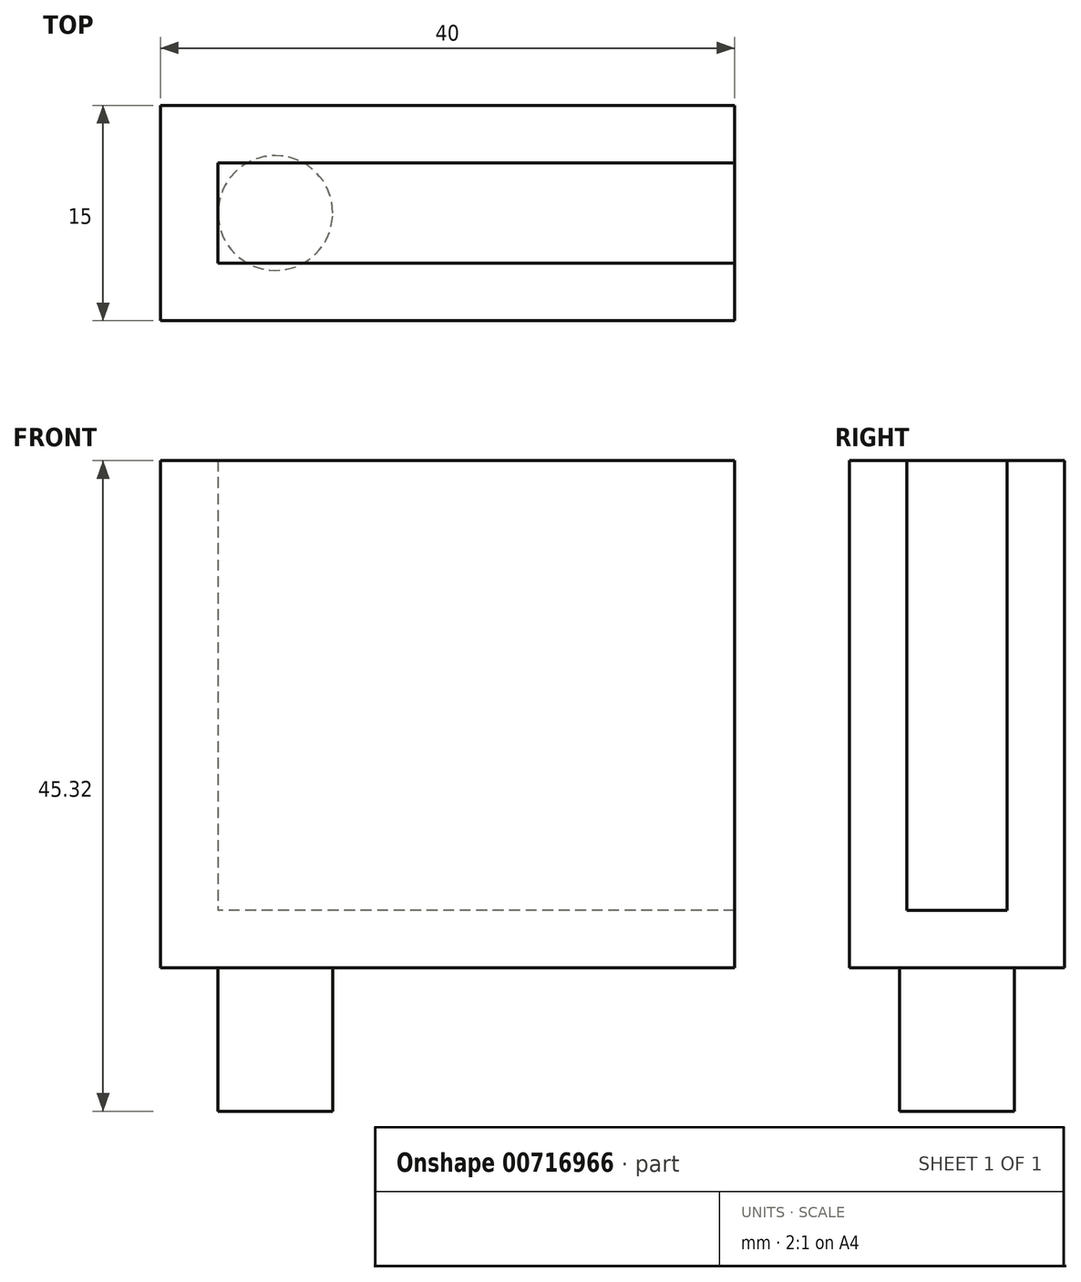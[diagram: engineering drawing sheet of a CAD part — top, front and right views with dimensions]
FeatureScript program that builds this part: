
annotation { "Feature Type Name" : "Feature", "Feature Type Description" : "" }
export const myFeature = defineFeature(function(context is Context, id is Id, definition is map)
    precondition{}
    {
        {
            var Q0;
            Q0=qCreatedBy(makeId("Front.planeOp"),FACE);
            var sketch = newSketch(context, id + "F0", { "sketchPlane" : qUnion([Q0])});
            skLineSegment(sketch, "E0.bottom", {"start": v(0, 0) * mm, "end": v(40, 0) * mm});
            skLineSegment(sketch, "E0.top", {"start": v(0, 35.32) * mm, "end": v(40, 35.32) * mm});
            skLineSegment(sketch, "E0.left", {"start": v(0, 0) * mm, "end": v(0, 35.32) * mm});
            skLineSegment(sketch, "E0.right", {"start": v(40, 0) * mm, "end": v(40, 35.32) * mm});
            skSolve(sketch);
        }
        {
            var Q0;
            Q0 = qSketchRegion(id + "F0", true);
            extrude(context, id + "F1", {"entities" : qUnion([Q0]), "endBound" : BoundingType.SYMMETRIC, "depth" : (7 + 8) * mm, "offsetDistance" : 25 * mm});
        }
        {
            var Q0;
            Q0=qCreatedBy(makeId("Front.planeOp"),FACE);
            var sketch = newSketch(context, id + "F2", { "sketchPlane" : qUnion([Q0])});
            skLineSegment(sketch, "E1.bottom", {"start": v(40, 35.32) * mm, "end": v(4, 35.32) * mm});
            skLineSegment(sketch, "E1.top", {"start": v(40, 4) * mm, "end": v(4, 4) * mm});
            skLineSegment(sketch, "E1.left", {"start": v(40, 35.32) * mm, "end": v(40, 4) * mm});
            skLineSegment(sketch, "E1.right", {"start": v(4, 35.32) * mm, "end": v(4, 4) * mm});
            skSolve(sketch);
        }
        {
            var Q0;
            Q0 = qSketchRegion(id + "F2", true);
            extrude(context, id + "F3", {"entities" : qUnion([Q0]), "operationType" : NewBodyOperationType.REMOVE, "endBound" : BoundingType.SYMMETRIC, "oppositeDirection" : true, "depth" : 7 * mm, "offsetDistance" : 25 * mm});
        }
        {
            var Q0;
            Q0=makeQuery(id+"F1.opExtrude","SWEPT_FACE",FACE,{"disambiguationData":[OSD([sQuery(id+"F0.wireOp",EDGE,"E0.bottom")])]});
            var sketch = newSketch(context, id + "F4", { "sketchPlane" : qUnion([Q0])});
            skCircle(sketch, "E2", {"center": v(8, 0) * mm, "radius": 4 * mm});
            skSolve(sketch);
        }
        {
            var Q0;
            Q0=makeQuery(id+"F4.imprint","IMPRINT",FACE,{"disambiguationData":[TD([[makeQuery(id+"F4.imprint","IMPRINT",EDGE,{"derivedFrom":sQuery(id+"F4.wireOp",EDGE,"E2")}),1.0]])]});
            extrude(context, id + "F5", {"entities" : qUnion([Q0]), "operationType" : NewBodyOperationType.ADD, "depth" : 10 * mm, "offsetDistance" : 25 * mm});
        }
    });
